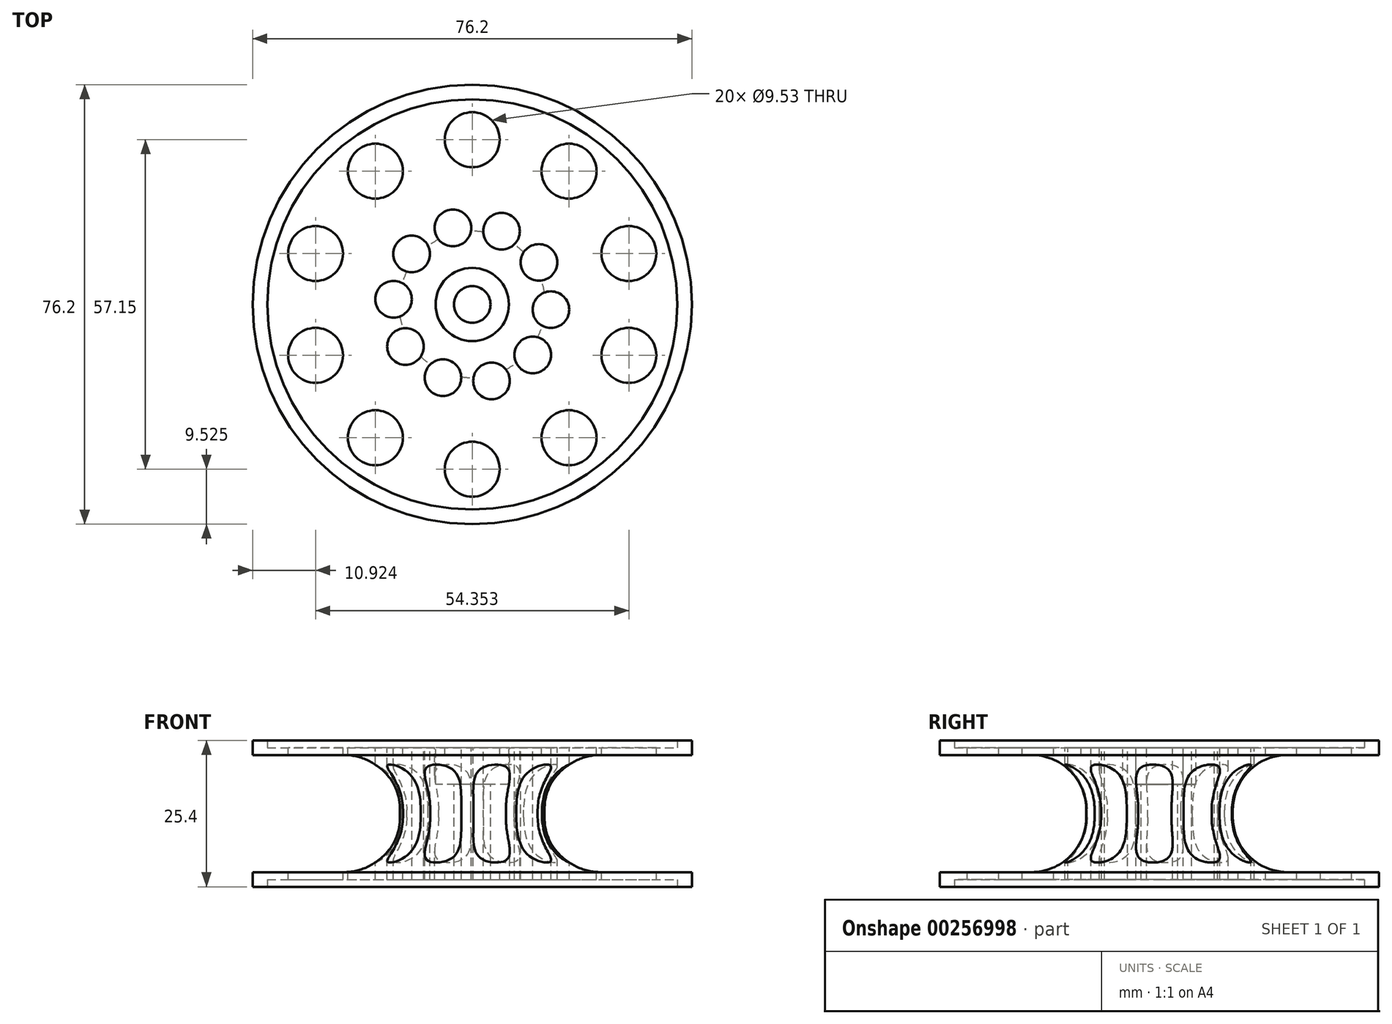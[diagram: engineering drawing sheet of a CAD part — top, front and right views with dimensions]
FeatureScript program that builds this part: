
annotation { "Feature Type Name" : "Feature", "Feature Type Description" : "" }
export const myFeature = defineFeature(function(context is Context, id is Id, definition is map)
    precondition{}
    {
        {
            var Q0;
            Q0=qCreatedBy(makeId("Front.planeOp"),FACE);
            var sketch = newSketch(context, id + "F0", { "sketchPlane" : qUnion([Q0])});
            skLineSegment(sketch, "E0", {"start": v(38.1, 25.4) * mm, "end": v(38.1, 22.86) * mm});
            skLineSegment(sketch, "E1", {"start": v(38.1, 22.86) * mm, "end": v(22.22, 22.86) * mm});
            skLineSegment(sketch, "E2", {"start": v(12.7, 13.33) * mm, "end": v(12.7, 12.06) * mm});
            skLineSegment(sketch, "E3", {"start": v(22.23, 2.54) * mm, "end": v(38.1, 2.54) * mm});
            skLineSegment(sketch, "E4", {"start": v(38.1, 2.54) * mm, "end": v(38.1, 0) * mm});
            skPoint(sketch, "E5.visualSharp", {"position": v(12.7, 22.86) * mm});
            skArc(sketch, "E5.filletArc", {"start": v(22.22, 22.86) * mm, "mid": v(15.49, 20.07) * mm, "end": v(12.7, 13.33) * mm});
            skPoint(sketch, "E6.visualSharp", {"position": v(12.7, 2.54) * mm});
            skArc(sketch, "E6.filletArc", {"start": v(12.7, 12.06) * mm, "mid": v(15.49, 5.33) * mm, "end": v(22.23, 2.54) * mm});
            skLineSegment(sketch, "E7", {"start": v(0, 25.4) * mm, "end": v(0, 48.13) * mm, "construction": true});
            skLineSegment(sketch, "E8.top", {"start": v(0, 24.13) * mm, "end": v(35.56, 24.13) * mm});
            skLineSegment(sketch, "E8.right", {"start": v(35.56, 25.4) * mm, "end": v(35.56, 24.13) * mm});
            skLineSegment(sketch, "E9.top", {"start": v(0, 1.27) * mm, "end": v(35.56, 1.27) * mm});
            skLineSegment(sketch, "E9.left", {"start": v(0, 0) * mm, "end": v(0, 1.27) * mm});
            skLineSegment(sketch, "E9.right", {"start": v(35.56, 0) * mm, "end": v(35.56, 1.27) * mm});
            skLineSegment(sketch, "E10", {"start": v(0, 24.13) * mm, "end": v(0, 1.27) * mm});
            skLineSegment(sketch, "E11", {"start": v(35.56, 0) * mm, "end": v(38.1, 0) * mm});
            skLineSegment(sketch, "E12", {"start": v(35.56, 25.4) * mm, "end": v(38.1, 25.4) * mm});
            skSolve(sketch);
        }
        {
            var Q0;
            Q0=makeQuery(id+"F0.imprint","IMPRINT",FACE,{"disambiguationData":[TD([[makeQuery(id+"F0.imprint","IMPRINT",EDGE,{"derivedFrom":sQuery(id+"F0.wireOp",EDGE,"YhaGrJna-TbGx-Yxnp-d4jX-ipEjyt3d0C8c")}),-1.0]])]});
            var Q1;
            Q1=makeQuery(id+"F0.imprint","IMPRINT",FACE,{"disambiguationData":[TD([[makeQuery(id+"F0.imprint","IMPRINT",EDGE,{"derivedFrom":sQuery(id+"F0.wireOp",EDGE,"E0")}),-1.0]])]});
            var Q2;
            Q2=sQuery(id+"F0.wireOp",EDGE,"E7");
            revolve(context, id + "F1", {"entities" : qUnion([Q0, Q1]), "axis" : qUnion([Q2]), "revolveType" : RevolveType.FULL});
        }
        {
            var Q0;
            Q0=makeQuery(id+"F1.opRevolve","SWEPT_FACE",FACE,{"disambiguationData":[OSD([sQuery(id+"F0.wireOp",EDGE,"E8.top")])]});
            var sketch = newSketch(context, id + "F2", { "sketchPlane" : qUnion([Q0])});
            skCircle(sketch, "E13", {"center": v(0, 28.58) * mm, "radius": 4.76 * mm});
            skCircle(sketch, "E14", {"center": v(5.08, 12.7) * mm, "radius": 3.18 * mm});
            skCircle(sketch, "E15.1.0", {"center": v(-16.8, 23.12) * mm, "radius": 4.76 * mm});
            skCircle(sketch, "E15.1.1", {"center": v(-3.36, 13.26) * mm, "radius": 3.18 * mm});
            skCircle(sketch, "E15.2.0", {"center": v(-27.18, 8.83) * mm, "radius": 4.76 * mm});
            skCircle(sketch, "E15.2.1", {"center": v(-10.5, 8.76) * mm, "radius": 3.18 * mm});
            skCircle(sketch, "E15.3.0", {"center": v(-27.18, -8.83) * mm, "radius": 4.76 * mm});
            skCircle(sketch, "E15.3.1", {"center": v(-13.65, 0.9) * mm, "radius": 3.18 * mm});
            skCircle(sketch, "E15.4.0", {"center": v(-16.8, -23.12) * mm, "radius": 4.76 * mm});
            skCircle(sketch, "E15.4.1", {"center": v(-11.57, -7.29) * mm, "radius": 3.18 * mm});
            skCircle(sketch, "E15.5.0", {"center": v(0, -28.58) * mm, "radius": 4.76 * mm});
            skCircle(sketch, "E15.5.1", {"center": v(-5.08, -12.7) * mm, "radius": 3.18 * mm});
            skCircle(sketch, "E15.6.0", {"center": v(16.8, -23.12) * mm, "radius": 4.76 * mm});
            skCircle(sketch, "E15.6.1", {"center": v(3.36, -13.26) * mm, "radius": 3.18 * mm});
            skCircle(sketch, "E15.7.0", {"center": v(27.18, -8.83) * mm, "radius": 4.76 * mm});
            skCircle(sketch, "E15.7.1", {"center": v(10.5, -8.76) * mm, "radius": 3.18 * mm});
            skCircle(sketch, "E15.8.0", {"center": v(27.18, 8.83) * mm, "radius": 4.76 * mm});
            skCircle(sketch, "E15.8.1", {"center": v(13.65, -0.9) * mm, "radius": 3.18 * mm});
            skCircle(sketch, "E15.9.0", {"center": v(16.8, 23.12) * mm, "radius": 4.76 * mm});
            skCircle(sketch, "E15.9.1", {"center": v(11.57, 7.29) * mm, "radius": 3.18 * mm});
            skPoint(sketch, "E15.center", {"position": v(0, 0) * mm});
            skSolve(sketch);
        }
        {
            var Q0;
            Q0=makeQuery(id+"F2.imprint","IMPRINT",FACE,{"disambiguationData":[TD([[makeQuery(id+"F2.imprint","IMPRINT",EDGE,{"derivedFrom":sQuery(id+"F2.wireOp",EDGE,"E13")}),1.0]])]});
            var Q1;
            Q1=makeQuery(id+"F2.imprint","IMPRINT",FACE,{"disambiguationData":[TD([[makeQuery(id+"F2.imprint","IMPRINT",EDGE,{"derivedFrom":sQuery(id+"F2.wireOp",EDGE,"E15.9.0")}),1.0]])]});
            var Q2;
            Q2=makeQuery(id+"F2.imprint","IMPRINT",FACE,{"disambiguationData":[TD([[makeQuery(id+"F2.imprint","IMPRINT",EDGE,{"derivedFrom":sQuery(id+"F2.wireOp",EDGE,"E15.8.0")}),1.0]])]});
            var Q3;
            Q3=makeQuery(id+"F2.imprint","IMPRINT",FACE,{"disambiguationData":[TD([[makeQuery(id+"F2.imprint","IMPRINT",EDGE,{"derivedFrom":sQuery(id+"F2.wireOp",EDGE,"E15.7.0")}),1.0]])]});
            var Q4;
            Q4=makeQuery(id+"F2.imprint","IMPRINT",FACE,{"disambiguationData":[TD([[makeQuery(id+"F2.imprint","IMPRINT",EDGE,{"derivedFrom":sQuery(id+"F2.wireOp",EDGE,"E15.6.0")}),1.0]])]});
            var Q5;
            Q5=makeQuery(id+"F2.imprint","IMPRINT",FACE,{"disambiguationData":[TD([[makeQuery(id+"F2.imprint","IMPRINT",EDGE,{"derivedFrom":sQuery(id+"F2.wireOp",EDGE,"E15.5.0")}),1.0]])]});
            var Q6;
            Q6=makeQuery(id+"F2.imprint","IMPRINT",FACE,{"disambiguationData":[TD([[makeQuery(id+"F2.imprint","IMPRINT",EDGE,{"derivedFrom":sQuery(id+"F2.wireOp",EDGE,"E15.4.0")}),1.0]])]});
            var Q7;
            Q7=makeQuery(id+"F2.imprint","IMPRINT",FACE,{"disambiguationData":[TD([[makeQuery(id+"F2.imprint","IMPRINT",EDGE,{"derivedFrom":sQuery(id+"F2.wireOp",EDGE,"E15.3.0")}),1.0]])]});
            var Q8;
            Q8=makeQuery(id+"F2.imprint","IMPRINT",FACE,{"disambiguationData":[TD([[makeQuery(id+"F2.imprint","IMPRINT",EDGE,{"derivedFrom":sQuery(id+"F2.wireOp",EDGE,"E15.2.0")}),1.0]])]});
            var Q9;
            Q9=makeQuery(id+"F2.imprint","IMPRINT",FACE,{"disambiguationData":[TD([[makeQuery(id+"F2.imprint","IMPRINT",EDGE,{"derivedFrom":sQuery(id+"F2.wireOp",EDGE,"E15.1.0")}),1.0]])]});
            var Q10;
            Q10=makeQuery(id+"F2.imprint","IMPRINT",FACE,{"disambiguationData":[TD([[makeQuery(id+"F2.imprint","IMPRINT",EDGE,{"derivedFrom":sQuery(id+"F2.wireOp",EDGE,"E15.1.1")}),1.0]])]});
            var Q11;
            Q11=makeQuery(id+"F2.imprint","IMPRINT",FACE,{"disambiguationData":[TD([[makeQuery(id+"F2.imprint","IMPRINT",EDGE,{"derivedFrom":sQuery(id+"F2.wireOp",EDGE,"E15.2.1")}),1.0]])]});
            var Q12;
            Q12=makeQuery(id+"F2.imprint","IMPRINT",FACE,{"disambiguationData":[TD([[makeQuery(id+"F2.imprint","IMPRINT",EDGE,{"derivedFrom":sQuery(id+"F2.wireOp",EDGE,"E15.3.1")}),1.0]])]});
            var Q13;
            Q13=makeQuery(id+"F2.imprint","IMPRINT",FACE,{"disambiguationData":[TD([[makeQuery(id+"F2.imprint","IMPRINT",EDGE,{"derivedFrom":sQuery(id+"F2.wireOp",EDGE,"E15.4.1")}),1.0]])]});
            var Q14;
            Q14=makeQuery(id+"F2.imprint","IMPRINT",FACE,{"disambiguationData":[TD([[makeQuery(id+"F2.imprint","IMPRINT",EDGE,{"derivedFrom":sQuery(id+"F2.wireOp",EDGE,"E15.5.1")}),1.0]])]});
            var Q15;
            Q15=makeQuery(id+"F2.imprint","IMPRINT",FACE,{"disambiguationData":[TD([[makeQuery(id+"F2.imprint","IMPRINT",EDGE,{"derivedFrom":sQuery(id+"F2.wireOp",EDGE,"E15.6.1")}),1.0]])]});
            var Q16;
            Q16=makeQuery(id+"F2.imprint","IMPRINT",FACE,{"disambiguationData":[TD([[makeQuery(id+"F2.imprint","IMPRINT",EDGE,{"derivedFrom":sQuery(id+"F2.wireOp",EDGE,"E15.7.1")}),1.0]])]});
            var Q17;
            Q17=makeQuery(id+"F2.imprint","IMPRINT",FACE,{"disambiguationData":[TD([[makeQuery(id+"F2.imprint","IMPRINT",EDGE,{"derivedFrom":sQuery(id+"F2.wireOp",EDGE,"E15.8.1")}),1.0]])]});
            var Q18;
            Q18=makeQuery(id+"F2.imprint","IMPRINT",FACE,{"disambiguationData":[TD([[makeQuery(id+"F2.imprint","IMPRINT",EDGE,{"derivedFrom":sQuery(id+"F2.wireOp",EDGE,"E15.9.1")}),1.0]])]});
            var Q19;
            Q19=makeQuery(id+"F2.imprint","IMPRINT",FACE,{"disambiguationData":[TD([[makeQuery(id+"F2.imprint","IMPRINT",EDGE,{"derivedFrom":sQuery(id+"F2.wireOp",EDGE,"E14")}),1.0]])]});
            extrude(context, id + "F3", {"entities" : qUnion([Q0, Q1, Q2, Q3, Q4, Q5, Q6, Q7, Q8, Q9, Q10, Q11, Q12, Q13, Q14, Q15, Q16, Q17, Q18, Q19]), "operationType" : NewBodyOperationType.REMOVE, "endBound" : BoundingType.THROUGH_ALL, "oppositeDirection" : true, "depth" : 25.4 * mm});
        }
        {
            var Q0;
            Q0=makeQuery(id+"F1.opRevolve","SWEPT_FACE",FACE,{"disambiguationData":[OSD([sQuery(id+"F0.wireOp",EDGE,"E8.top")])]});
            var sketch = newSketch(context, id + "F4", { "sketchPlane" : qUnion([Q0])});
            skCircle(sketch, "E16", {"center": v(0, 0) * mm, "radius": 6.35 * mm});
            skSolve(sketch);
        }
        {
            var Q0;
            Q0=makeQuery(id+"F4.imprint","IMPRINT",FACE,{"disambiguationData":[TD([[makeQuery(id+"F4.imprint","IMPRINT",EDGE,{"derivedFrom":sQuery(id+"F4.wireOp",EDGE,"E16")}),1.0]])]});
            extrude(context, id + "F5", {"entities" : qUnion([Q0]), "operationType" : NewBodyOperationType.REMOVE, "oppositeDirection" : true, "depth" : 6.35 * mm});
        }
        {
            var Q0;
            Q0=makeQuery(id+"F5.boolean.opBoolean","COPY",FACE,{"derivedFrom":makeQuery(id+"F5.opExtrude","CAP_FACE",FACE,{"disambiguationData":[OSD([sQuery(id+"F4.wireOp",EDGE,"E16")])],"isStart":false})});
            var sketch = newSketch(context, id + "F6", { "sketchPlane" : qUnion([Q0])});
            skCircle(sketch, "E17", {"center": v(0, 0) * mm, "radius": 3.18 * mm});
            skSolve(sketch);
        }
        {
            var Q0;
            Q0=makeQuery(id+"F6.imprint","IMPRINT",FACE,{"disambiguationData":[TD([[makeQuery(id+"F6.imprint","IMPRINT",EDGE,{"derivedFrom":sQuery(id+"F6.wireOp",EDGE,"E17")}),1.0]])]});
            extrude(context, id + "F7", {"entities" : qUnion([Q0]), "operationType" : NewBodyOperationType.REMOVE, "endBound" : BoundingType.THROUGH_ALL, "oppositeDirection" : true, "depth" : 25.4 * mm});
        }
    });
